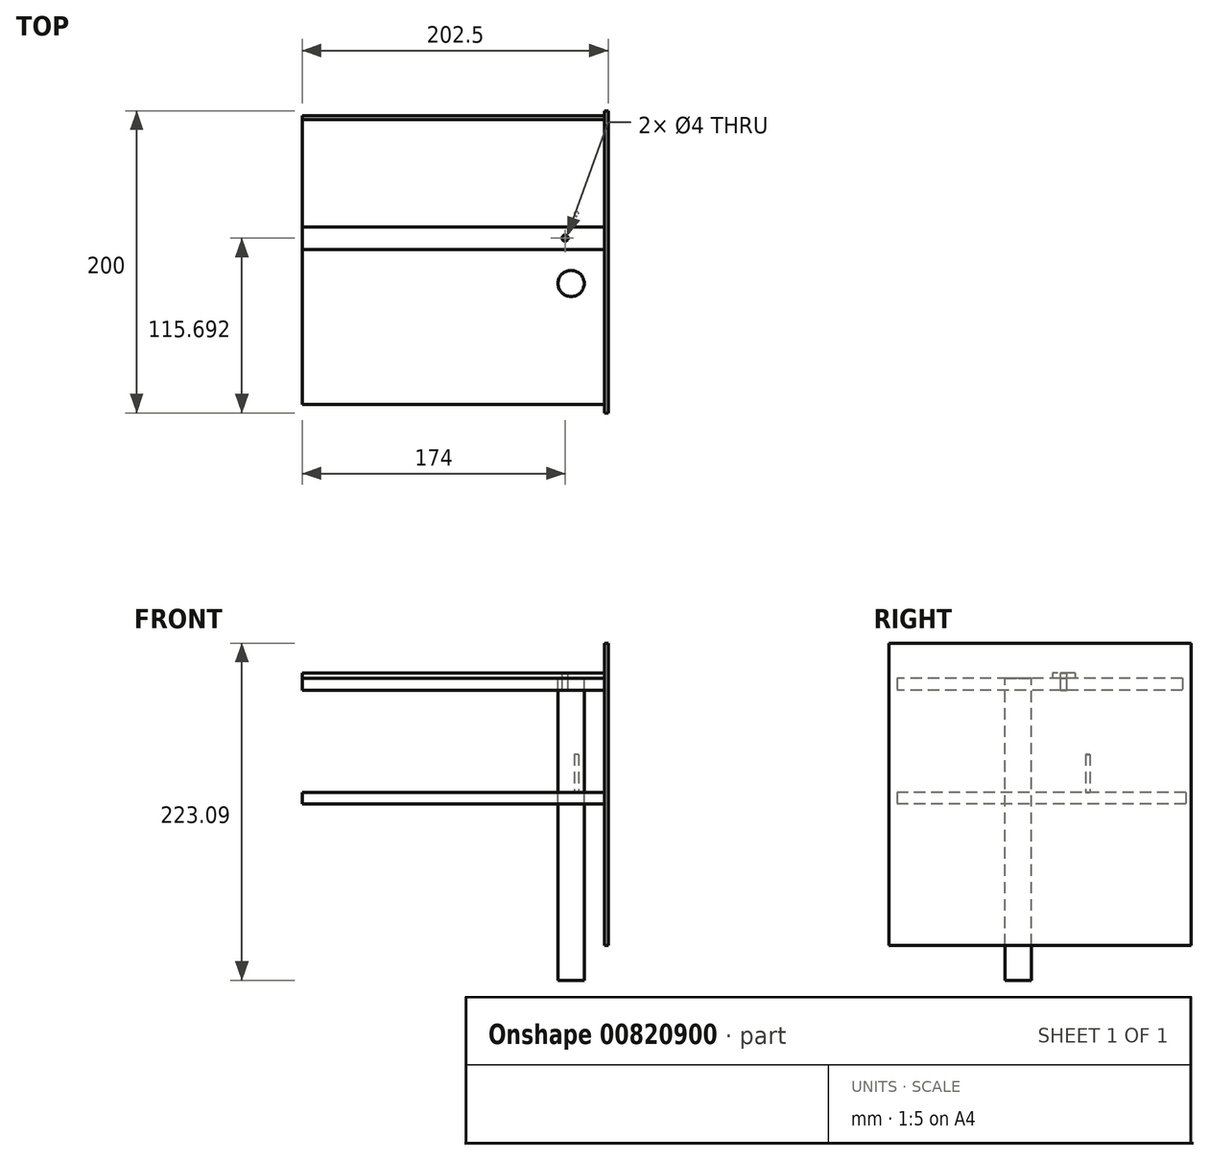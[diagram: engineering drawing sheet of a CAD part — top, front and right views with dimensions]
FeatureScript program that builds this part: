
annotation { "Feature Type Name" : "Feature", "Feature Type Description" : "" }
export const myFeature = defineFeature(function(context is Context, id is Id, definition is map)
    precondition{}
    {
        {
            var Q0;
            Q0=qCreatedBy(makeId("Right.planeOp"),FACE);
            var sketch = newSketch(context, id + "F0", { "sketchPlane" : qUnion([Q0])});
            skLineSegment(sketch, "E0.bottom", {"start": v(0, 200) * mm, "end": v(200, 200) * mm});
            skLineSegment(sketch, "E0.top", {"start": v(0, 0) * mm, "end": v(200, 0) * mm});
            skLineSegment(sketch, "E0.left", {"start": v(0, 200) * mm, "end": v(0, 0) * mm});
            skLineSegment(sketch, "E0.right", {"start": v(200, 200) * mm, "end": v(200, 0) * mm});
            skSolve(sketch);
        }
        {
            var Q0;
            Q0=makeQuery(id+"F0.imprint","IMPRINT",FACE,{"disambiguationData":[TD([[makeQuery(id+"F0.imprint","IMPRINT",EDGE,{"derivedFrom":sQuery(id+"F0.wireOp",EDGE,"E0.bottom")}),-1.0]])]});
            extrude(context, id + "F1", {"entities" : qUnion([Q0]), "depth" : 2.5 * mm, "offsetDistance" : 25 * mm});
        }
        {
            var Q0;
            Q0=makeQuery(id+"F1.opExtrude","CAP_FACE",FACE,{"disambiguationData":[OSD([sQuery(id+"F0.wireOp",EDGE,"E0.bottom"),sQuery(id+"F0.wireOp",EDGE,"E0.top"),sQuery(id+"F0.wireOp",EDGE,"E0.left"),sQuery(id+"F0.wireOp",EDGE,"E0.right")])],"isStart":true});
            var sketch = newSketch(context, id + "F2", { "sketchPlane" : qUnion([Q0])});
            skLineSegment(sketch, "E1.bottom", {"start": v(-123.22, 180.38) * mm, "end": v(-108.22, 180.38) * mm});
            skLineSegment(sketch, "E1.top", {"start": v(-123.22, 176.9) * mm, "end": v(-108.22, 176.9) * mm});
            skLineSegment(sketch, "E1.left", {"start": v(-123.22, 180.38) * mm, "end": v(-123.22, 176.9) * mm});
            skLineSegment(sketch, "E1.right", {"start": v(-108.22, 180.38) * mm, "end": v(-108.22, 176.9) * mm});
            skSolve(sketch);
        }
        {
            var Q0;
            Q0=makeQuery(id+"F2.imprint","IMPRINT",FACE,{"disambiguationData":[TD([[makeQuery(id+"F2.imprint","IMPRINT",EDGE,{"derivedFrom":sQuery(id+"F2.wireOp",EDGE,"E1.bottom")}),-1.0]])]});
            extrude(context, id + "F3", {"entities" : qUnion([Q0]), "depth" : 200 * mm, "offsetDistance" : 25 * mm});
        }
        {
            var Q0;
            Q0=makeQuery(id+"F1.opExtrude","CAP_FACE",FACE,{"disambiguationData":[OSD([sQuery(id+"F0.wireOp",EDGE,"E0.bottom"),sQuery(id+"F0.wireOp",EDGE,"E0.top"),sQuery(id+"F0.wireOp",EDGE,"E0.left"),sQuery(id+"F0.wireOp",EDGE,"E0.right")])],"isStart":true});
            var sketch = newSketch(context, id + "F4", { "sketchPlane" : qUnion([Q0])});
            skLineSegment(sketch, "E2.bottom", {"start": v(-194.34, 176.9) * mm, "end": v(-5.54, 176.9) * mm});
            skLineSegment(sketch, "E2.top", {"start": v(-194.34, 168.9) * mm, "end": v(-5.54, 168.9) * mm});
            skLineSegment(sketch, "E2.left", {"start": v(-194.34, 176.9) * mm, "end": v(-194.34, 168.9) * mm});
            skLineSegment(sketch, "E2.right", {"start": v(-5.54, 176.9) * mm, "end": v(-5.54, 168.9) * mm});
            skSolve(sketch);
        }
        {
            var Q0;
            Q0=makeQuery(id+"F4.imprint","IMPRINT",FACE,{"disambiguationData":[TD([[makeQuery(id+"F4.imprint","IMPRINT",EDGE,{"derivedFrom":sQuery(id+"F4.wireOp",EDGE,"E2.bottom")}),-1.0]])]});
            extrude(context, id + "F5", {"entities" : qUnion([Q0]), "depth" : 200 * mm, "offsetDistance" : 25 * mm});
        }
        {
            var Q0;
            Q0=makeQuery(id+"F3.opExtrude","SWEPT_FACE",FACE,{"disambiguationData":[OSD([sQuery(id+"F2.wireOp",EDGE,"E1.bottom")])]});
            var sketch = newSketch(context, id + "F6", { "sketchPlane" : qUnion([Q0])});
            skCircle(sketch, "E3", {"center": v(-26, 115.7) * mm, "radius": 2 * mm});
            skSolve(sketch);
        }
        {
            var Q0;
            Q0=makeQuery(id+"F6.imprint","IMPRINT",FACE,{"disambiguationData":[TD([[makeQuery(id+"F6.imprint","IMPRINT",EDGE,{"derivedFrom":sQuery(id+"F6.wireOp",EDGE,"E3")}),1.0]])]});
            extrude(context, id + "F7", {"entities" : qUnion([Q0]), "operationType" : NewBodyOperationType.REMOVE, "endBound" : BoundingType.THROUGH_ALL, "oppositeDirection" : true, "depth" : 25 * mm, "offsetDistance" : 25 * mm});
        }
        {
            var Q0;
            Q0=makeQuery(id+"F5.opExtrude","SWEPT_FACE",FACE,{"disambiguationData":[OSD([sQuery(id+"F4.wireOp",EDGE,"E2.bottom")])]});
            var sketch = newSketch(context, id + "F8", { "sketchPlane" : qUnion([Q0])});
            skCircle(sketch, "E4", {"center": v(-22, 85.7) * mm, "radius": 8.66 * mm});
            skCircle(sketch, "E5.0", {"center": v(-26, 115.7) * mm, "radius": 2 * mm});
            skSolve(sketch);
        }
        {
            var Q0;
            Q0=makeQuery(id+"F8.imprint","IMPRINT",FACE,{"disambiguationData":[TD([[makeQuery(id+"F8.imprint","IMPRINT",EDGE,{"derivedFrom":sQuery(id+"F8.wireOp",EDGE,"E4")}),1.0]])]});
            extrude(context, id + "F9", {"entities" : qUnion([Q0]), "oppositeDirection" : true, "depth" : 200 * mm, "offsetDistance" : 25 * mm});
        }
        {
            var Q0;
            Q0=makeQuery(id+"F1.opExtrude","CAP_FACE",FACE,{"disambiguationData":[OSD([sQuery(id+"F0.wireOp",EDGE,"E0.bottom"),sQuery(id+"F0.wireOp",EDGE,"E0.top"),sQuery(id+"F0.wireOp",EDGE,"E0.left"),sQuery(id+"F0.wireOp",EDGE,"E0.right")])],"isStart":true});
            var sketch = newSketch(context, id + "F10", { "sketchPlane" : qUnion([Q0])});
            skLineSegment(sketch, "E6.bottom", {"start": v(-196.6, 101.4) * mm, "end": v(-5.53, 101.4) * mm});
            skLineSegment(sketch, "E6.top", {"start": v(-196.6, 93.64) * mm, "end": v(-5.53, 93.64) * mm});
            skLineSegment(sketch, "E6.left", {"start": v(-196.6, 101.4) * mm, "end": v(-196.6, 93.64) * mm});
            skLineSegment(sketch, "E6.right", {"start": v(-5.53, 101.4) * mm, "end": v(-5.53, 93.64) * mm});
            skSolve(sketch);
        }
        {
            var Q0;
            Q0=makeQuery(id+"F10.imprint","IMPRINT",FACE,{"disambiguationData":[TD([[makeQuery(id+"F10.imprint","IMPRINT",EDGE,{"derivedFrom":sQuery(id+"F10.wireOp",EDGE,"E6.bottom")}),-1.0]])]});
            extrude(context, id + "F11", {"entities" : qUnion([Q0]), "depth" : 200 * mm, "offsetDistance" : 25 * mm});
        }
        {
            var Q0;
            Q0=makeQuery(id+"F11.opExtrude","SWEPT_FACE",FACE,{"disambiguationData":[OSD([sQuery(id+"F10.wireOp",EDGE,"E6.bottom")])]});
            var sketch = newSketch(context, id + "F12", { "sketchPlane" : qUnion([Q0])});
            skCircle(sketch, "E7", {"center": v(-18.5, 131.7) * mm, "radius": 1.5 * mm});
            skCircle(sketch, "E8.0.0", {"center": v(-22, 85.7) * mm, "radius": 8.66 * mm});
            skSolve(sketch);
        }
        {
            var Q0;
            Q0=makeQuery(id+"F12.imprint","IMPRINT",FACE,{"disambiguationData":[TD([[makeQuery(id+"F12.imprint","IMPRINT",EDGE,{"derivedFrom":sQuery(id+"F12.wireOp",EDGE,"E7")}),1.0]])]});
            extrude(context, id + "F13", {"entities" : qUnion([Q0]), "depth" : 25 * mm, "offsetDistance" : 25 * mm});
        }
    });
